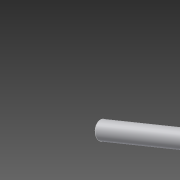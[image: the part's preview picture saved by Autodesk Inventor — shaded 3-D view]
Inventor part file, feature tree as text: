
AUTODESK INVENTOR PART (.ipt)
format: ipt  version: 2013 (Build 170138000, 138)  size: 60,928 bytes
history: native  units: mm
features: extrude x1, sketch x1
ambient origin geometry x8: Origin, YZ Plane, XZ Plane, XY Plane, X Axis, Y Axis, Z Axis, Center Point
bodies: Volumenkörper1 (feature_tree)
feature tree (2):
  extrude  "Extrusion1"  Depth=3.9mm TaperAngle=0.0deg
  sketch  "Skizze1"  dims[d0=1.5mm d1=3.9mm d2=0.0mm]
